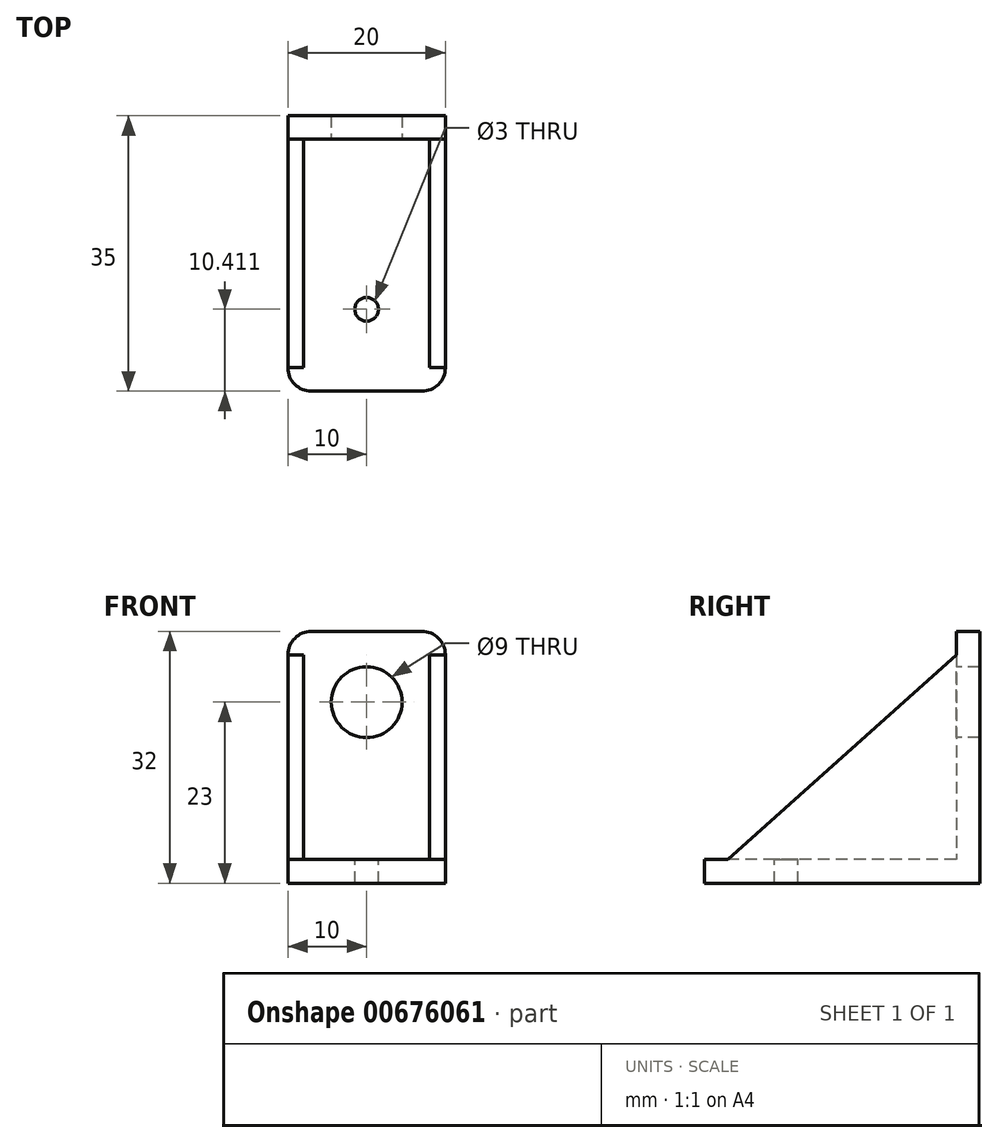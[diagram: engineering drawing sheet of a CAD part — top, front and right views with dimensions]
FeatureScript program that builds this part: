
annotation { "Feature Type Name" : "Feature", "Feature Type Description" : "" }
export const myFeature = defineFeature(function(context is Context, id is Id, definition is map)
    precondition{}
    {
        {
            var Q0;
            Q0=qCreatedBy(makeId("Top.planeOp"),FACE);
            var sketch = newSketch(context, id + "F0", { "sketchPlane" : qUnion([Q0])});
            skLineSegment(sketch, "E0.bottom", {"start": v(0, 0) * mm, "end": v(20, 0) * mm});
            skLineSegment(sketch, "E0.top", {"start": v(3, -32) * mm, "end": v(17, -32) * mm});
            skLineSegment(sketch, "E0.left", {"start": v(0, 0) * mm, "end": v(0, -29) * mm});
            skLineSegment(sketch, "E0.right", {"start": v(20, 0) * mm, "end": v(20, -29) * mm});
            skPoint(sketch, "E1.visualSharp", {"position": v(0, -32) * mm});
            skArc(sketch, "E1.filletArc", {"start": v(0, -29) * mm, "mid": v(0.88, -31.12) * mm, "end": v(3, -32) * mm});
            skPoint(sketch, "E2.visualSharp", {"position": v(20, -32) * mm});
            skArc(sketch, "E2.filletArc", {"start": v(17, -32) * mm, "mid": v(19.12, -31.12) * mm, "end": v(20, -29) * mm});
            skSolve(sketch);
        }
        {
            var Q0;
            Q0 = qSketchRegion(id + "F0", true);
            extrude(context, id + "F1", {"entities" : qUnion([Q0]), "depth" : 3 * mm, "offsetDistance" : 25 * mm});
        }
        {
            var Q0;
            Q0=makeQuery(id+"F1.opExtrude","SWEPT_FACE",FACE,{"disambiguationData":[OSD([sQuery(id+"F0.wireOp",EDGE,"E0.bottom")])]});
            var sketch = newSketch(context, id + "F2", { "sketchPlane" : qUnion([Q0])});
            skLineSegment(sketch, "E3.bottom", {"start": v(0, 0) * mm, "end": v(-20, 0) * mm});
            skLineSegment(sketch, "E3.top", {"start": v(-3, 32) * mm, "end": v(-17, 32) * mm});
            skLineSegment(sketch, "E3.left", {"start": v(0, 0) * mm, "end": v(0, 29) * mm});
            skLineSegment(sketch, "E3.right", {"start": v(-20, 0) * mm, "end": v(-20, 29) * mm});
            skPoint(sketch, "E4.visualSharp", {"position": v(0, 32) * mm});
            skArc(sketch, "E4.filletArc", {"start": v(0, 29) * mm, "mid": v(-0.88, 31.12) * mm, "end": v(-3, 32) * mm});
            skPoint(sketch, "E5.visualSharp", {"position": v(-20, 32) * mm});
            skArc(sketch, "E5.filletArc", {"start": v(-17, 32) * mm, "mid": v(-19.12, 31.12) * mm, "end": v(-20, 29) * mm});
            skSolve(sketch);
        }
        {
            var Q0;
            Q0 = qSketchRegion(id + "F2", true);
            extrude(context, id + "F3", {"entities" : qUnion([Q0]), "operationType" : NewBodyOperationType.ADD, "depth" : 3 * mm, "offsetDistance" : 25 * mm});
        }
        {
            var Q0;
            Q0=makeQuery(id+"F3.boolean.opBoolean","MERGE",FACE,{"derivedFrom":[makeQuery(id+"F1.opExtrude","SWEPT_FACE",FACE,{"disambiguationData":[OSD([sQuery(id+"F0.wireOp",EDGE,"E0.left")])]}),makeQuery(id+"F3.opExtrude","SWEPT_FACE",FACE,{"disambiguationData":[OSD([sQuery(id+"F2.wireOp",EDGE,"E3.left")])]})]});
            var sketch = newSketch(context, id + "F4", { "sketchPlane" : qUnion([Q0])});
            skLineSegment(sketch, "E6", {"start": v(0, 29) * mm, "end": v(29, 3) * mm});
            skLineSegment(sketch, "E7", {"start": v(29, 3) * mm, "end": v(0, 3) * mm});
            skLineSegment(sketch, "E8", {"start": v(0, 3) * mm, "end": v(0, 29) * mm});
            skSolve(sketch);
        }
        {
            var Q0;
            Q0 = qSketchRegion(id + "F4", true);
            extrude(context, id + "F5", {"entities" : qUnion([Q0]), "operationType" : NewBodyOperationType.ADD, "oppositeDirection" : true, "depth" : 2 * mm, "offsetDistance" : 25 * mm});
        }
        {
            var Q0;
            Q0=makeQuery(id+"F3.boolean.opBoolean","MERGE",FACE,{"derivedFrom":[makeQuery(id+"F1.opExtrude","SWEPT_FACE",FACE,{"disambiguationData":[OSD([sQuery(id+"F0.wireOp",EDGE,"E0.right")])]}),makeQuery(id+"F3.opExtrude","SWEPT_FACE",FACE,{"disambiguationData":[OSD([sQuery(id+"F2.wireOp",EDGE,"E3.right")])]})]});
            var sketch = newSketch(context, id + "F6", { "sketchPlane" : qUnion([Q0])});
            skLineSegment(sketch, "E9", {"start": v(0, 29) * mm, "end": v(-29, 3) * mm});
            skLineSegment(sketch, "E10", {"start": v(-29, 3) * mm, "end": v(0, 3) * mm});
            skLineSegment(sketch, "E11", {"start": v(0, 3) * mm, "end": v(0, 29) * mm});
            skSolve(sketch);
        }
        {
            var Q0;
            Q0 = qSketchRegion(id + "F6", true);
            extrude(context, id + "F7", {"entities" : qUnion([Q0]), "operationType" : NewBodyOperationType.ADD, "oppositeDirection" : true, "depth" : 2 * mm, "offsetDistance" : 25 * mm});
        }
        {
            var Q0;
            Q0=makeQuery(id+"F1.opExtrude","CAP_FACE",FACE,{"disambiguationData":[OSD([sQuery(id+"F0.wireOp",EDGE,"E0.bottom"),sQuery(id+"F0.wireOp",EDGE,"E0.top"),sQuery(id+"F0.wireOp",EDGE,"E0.left"),sQuery(id+"F0.wireOp",EDGE,"E0.right"),sQuery(id+"F0.wireOp",EDGE,"E1.filletArc"),sQuery(id+"F0.wireOp",EDGE,"E2.filletArc")])],"isStart":false});
            var sketch = newSketch(context, id + "F8", { "sketchPlane" : qUnion([Q0])});
            skCircle(sketch, "E12", {"center": v(10, -21.59) * mm, "radius": 1.5 * mm});
            skSolve(sketch);
        }
        {
            var Q0;
            Q0=makeQuery(id+"F8.imprint","IMPRINT",FACE,{"disambiguationData":[TD([[makeQuery(id+"F8.imprint","IMPRINT",EDGE,{"derivedFrom":sQuery(id+"F8.wireOp",EDGE,"E12")}),1.0]])]});
            extrude(context, id + "F9", {"entities" : qUnion([Q0]), "operationType" : NewBodyOperationType.REMOVE, "oppositeDirection" : true, "depth" : 25 * mm, "offsetDistance" : 25 * mm});
        }
        {
            var Q0;
            Q0=makeQuery(id+"F3.opExtrude","CAP_FACE",FACE,{"disambiguationData":[OSD([sQuery(id+"F2.wireOp",EDGE,"E3.bottom"),sQuery(id+"F2.wireOp",EDGE,"E3.top"),sQuery(id+"F2.wireOp",EDGE,"E3.left"),sQuery(id+"F2.wireOp",EDGE,"E3.right"),sQuery(id+"F2.wireOp",EDGE,"E4.filletArc"),sQuery(id+"F2.wireOp",EDGE,"E5.filletArc")])],"isStart":true});
            var sketch = newSketch(context, id + "F10", { "sketchPlane" : qUnion([Q0])});
            skCircle(sketch, "E13", {"center": v(10, 23) * mm, "radius": 4.5 * mm});
            skSolve(sketch);
        }
        {
            var Q0;
            Q0=makeQuery(id+"F10.imprint","IMPRINT",FACE,{"disambiguationData":[TD([[makeQuery(id+"F10.imprint","IMPRINT",EDGE,{"derivedFrom":sQuery(id+"F10.wireOp",EDGE,"E13")}),1.0]])]});
            extrude(context, id + "F11", {"entities" : qUnion([Q0]), "operationType" : NewBodyOperationType.REMOVE, "oppositeDirection" : true, "depth" : 25 * mm, "offsetDistance" : 25 * mm});
        }
    });
